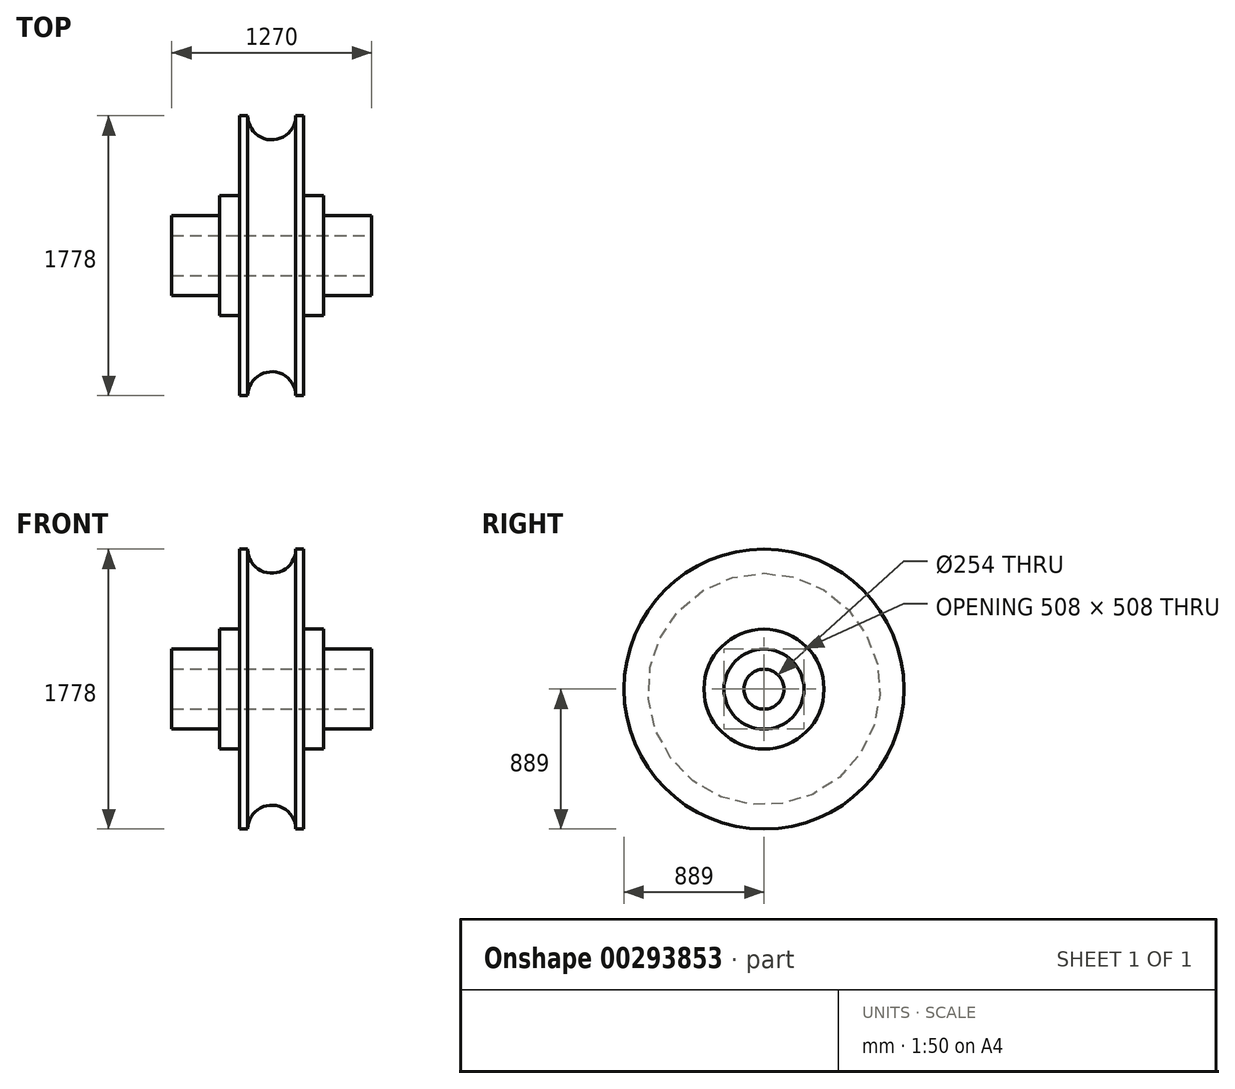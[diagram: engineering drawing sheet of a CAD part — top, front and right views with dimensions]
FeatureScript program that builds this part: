
annotation { "Feature Type Name" : "Feature", "Feature Type Description" : "" }
export const myFeature = defineFeature(function(context is Context, id is Id, definition is map)
    precondition{}
    {
        {
            var Q0;
            Q0=qCreatedBy(makeId("Front.planeOp"),FACE);
            var sketch = newSketch(context, id + "F0", { "sketchPlane" : qUnion([Q0])});
            skLineSegment(sketch, "E0", {"start": v(-330.2, 254) * mm, "end": v(330.2, 254) * mm});
            skLineSegment(sketch, "E1", {"start": v(330.2, 254) * mm, "end": v(330.2, 381) * mm});
            skLineSegment(sketch, "E2", {"start": v(330.2, 381) * mm, "end": v(203.2, 381) * mm});
            skLineSegment(sketch, "E3", {"start": v(203.2, 381) * mm, "end": v(203.2, 889) * mm});
            skLineSegment(sketch, "E4", {"start": v(203.2, 889) * mm, "end": v(152.4, 889) * mm});
            skLineSegment(sketch, "E5", {"start": v(-152.4, 889) * mm, "end": v(-203.2, 889) * mm});
            skLineSegment(sketch, "E6", {"start": v(-203.2, 889) * mm, "end": v(-203.2, 381) * mm});
            skLineSegment(sketch, "E7", {"start": v(-203.2, 381) * mm, "end": v(-330.2, 381) * mm});
            skLineSegment(sketch, "E8", {"start": v(-330.2, 381) * mm, "end": v(-330.2, 254) * mm});
            skArc(sketch, "E9", {"start": v(152.4, 889) * mm, "mid": v(0, 736.6) * mm, "end": v(-152.4, 889) * mm});
            skLineSegment(sketch, "E10", {"start": v(0, 0) * mm, "end": v(330.2, 0) * mm, "construction": true});
            skSolve(sketch);
        }
        {
            var Q0;
            Q0 = qSketchRegion(id + "F0", true);
            var Q1;
            Q1=sQuery(id+"F0.wireOp",EDGE,"E10");
            revolve(context, id + "F1", {"entities" : qUnion([Q0]), "axis" : qUnion([Q1]), "revolveType" : RevolveType.FULL});
        }
        {
            var Q0;
            Q0=qCreatedBy(makeId("Right.planeOp"),FACE);
            var sketch = newSketch(context, id + "F2", { "sketchPlane" : qUnion([Q0])});
            skCircle(sketch, "E11", {"center": v(0, 0) * mm, "radius": 254 * mm});
            skSolve(sketch);
        }
        {
            var Q0;
            Q0 = qSketchRegion(id + "F2", true);
            extrude(context, id + "F3", {"entities" : qUnion([Q0]), "operationType" : NewBodyOperationType.ADD, "endBound" : BoundingType.SYMMETRIC, "oppositeDirection" : true, "depth" : 1270 * mm});
        }
        {
            var Q0;
            Q0=makeQuery(id+"F3.opExtrude","CAP_FACE",FACE,{"disambiguationData":[OSD([sQuery(id+"F2.wireOp",EDGE,"E11")])],"isStart":true});
            var sketch = newSketch(context, id + "F4", { "sketchPlane" : qUnion([Q0])});
            skCircle(sketch, "E12", {"center": v(0, 0) * mm, "radius": 127 * mm});
            skSolve(sketch);
        }
        {
            var Q0;
            Q0 = qSketchRegion(id + "F4", true);
            extrude(context, id + "F5", {"entities" : qUnion([Q0]), "operationType" : NewBodyOperationType.REMOVE, "endBound" : BoundingType.THROUGH_ALL, "oppositeDirection" : true, "depth" : 25.4 * mm});
        }
    });
